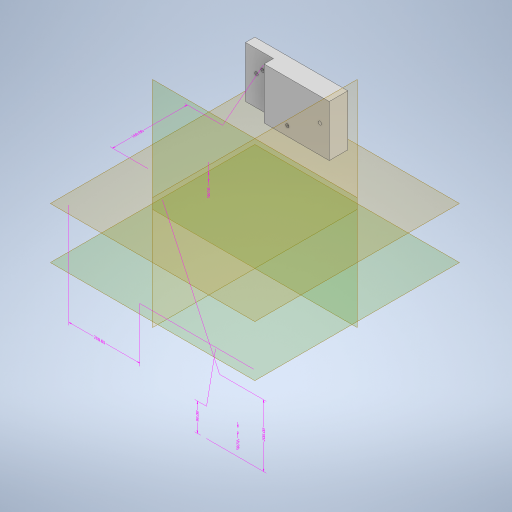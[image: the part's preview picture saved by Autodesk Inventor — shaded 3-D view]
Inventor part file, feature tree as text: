
AUTODESK INVENTOR PART (.ipt)
format: ipt  version: 2023 (Build 270158000, 158)  size: 446,976 bytes
history: native  units: mm
features: other x9, sketch x9, extrude x5, hole x4, plane x4, split x3
ambient origin geometry x8: Origin, YZ Plane, XZ Plane, XY Plane, X Axis, Y Axis, Z Axis, Center Point
bodies: Body1 (feature_tree)
feature tree (34):
  other  "Sólido1"
  other  "Anotaciones"
  extrude  "Extrusión1"  Depth=200.0mm
  hole  "Agujero1"  [1 undecoded]
  extrude  "Extrusión2"  Depth=15.0mm
  extrude  "Extrusión3"  Depth=20.0mm TaperAngle=0.0deg
  extrude  "Extrusión4"  Depth=200.0mm
  extrude  "Extrusión5"  Depth=20.0mm
  hole  "Agujero2"  [1 undecoded]
  plane  "Plano de trabajo1"
  split  "Dividir1"
  plane  "Plano de trabajo2"
  plane  "Plano de trabajo3"
  plane  "Plano de trabajo4"
  hole  "Agujero3"  [1 undecoded]
  hole  "Agujero4"  [1 undecoded]
  split  "Dividir2"
  split  "Dividir3"
  other  "Suprimir cara5"
  sketch  "Boceto2"  dims[d7=15.0mm d8=200.0mm]
  sketch  "Boceto3"  dims[d9=10.0mm d10=0.0mm]
  sketch  "Boceto4"  dims[d11=3.5mm d12=1.75mm d13=1.75mm d14=1.75mm d15=1.75mm d16=10.0mm d17=10.0mm d19=40.0mm]
  sketch  "Boceto5"  dims[d20=3.5mm d21=6.0mm d22=4.0mm d23=2.0mm d24=90.0deg d25=8.0mm d26=20.594885mm d27=15.0mm]
  sketch  "Boceto6"  dims[d28=20.0mm d29=80.0mm d30=0.0mm]
  sketch  "Boceto7"  dims[d31=57.0mm d32=200.0mm]
  sketch  "Boceto8"  dims[d33=110.0mm d34=0.0mm d36=20.0mm]
  sketch  "Boceto9"  dims[d37=20.0mm d38=20.0mm]
  sketch  "Boceto10"  dims[d39=90.0mm d40=0.0mm d43=30.0mm d44=0.0mm d45=3.5mm d46=1.75mm d47=1.75mm d48=1.75mm d49=1.75mm d50=10.0mm d51=10.0mm d52=15.0mm d53=10.0mm d54=10.0mm d55=15.0mm d56=3.5mm d57=6.0mm d58=4.0mm d59=2.0mm d60=90.0deg d61=8.0mm d62=20.594885mm d63=10.0mm d65=10.0mm d75=200.0mm d76=10.0mm d77=20.0mm d81=40.0mm d88=90.0deg d89=10.0mm d90=30.0mm d91=5.0mm d92=5.0mm d93=5.0mm d94=5.0mm d95=30.0mm d96=5.0mm d97=5.0mm d98=3.5mm d99=5.0mm d100=5.0mm d101=5.0mm d102=5.0mm d103=5.0mm d104=20.0mm d105=3.5mm d106=6.0mm d107=4.0mm d108=2.0mm d109=90.0deg d110=8.0mm d111=20.594885mm d112=10.0mm d113=30.0mm d114=5.0mm d115=5.0mm d116=5.0mm d117=5.0mm d118=5.0mm d119=5.0mm d120=3.5mm d121=5.0mm d122=5.0mm d123=5.0mm d124=5.0mm d125=5.0mm d126=30.0mm d127=30.0mm d128=3.5mm d129=6.0mm d130=4.0mm d131=2.0mm d132=90.0deg d133=8.0mm d134=20.594885mm d66=5.760865mm d67=7.72461mm d68=200.0mm d69=3.008686mm d70=2.422102mm d71=10.0mm d72=3.500509mm d73=2.402572mm d74=90.0mm d78=3.13122mm d79=6.269346mm d80=200.0mm d82=8.450127mm d83=0.968417mm d84=20.0mm d85=4.759975mm d86=4.646891mm d87=160.0mm]
  other  "Cota lineal 1"
  other  "Cota lineal 2"
  other  "Cota lineal 3"
  other  "Cota lineal 4"
  other  "Cota lineal 5"
  other  "Cota lineal 6"
note: 4 required parameter values undecoded (feature->parameter linkage not recoverable at this tier; creation-order binding heuristic only, values carry confidence <= 0.55)
